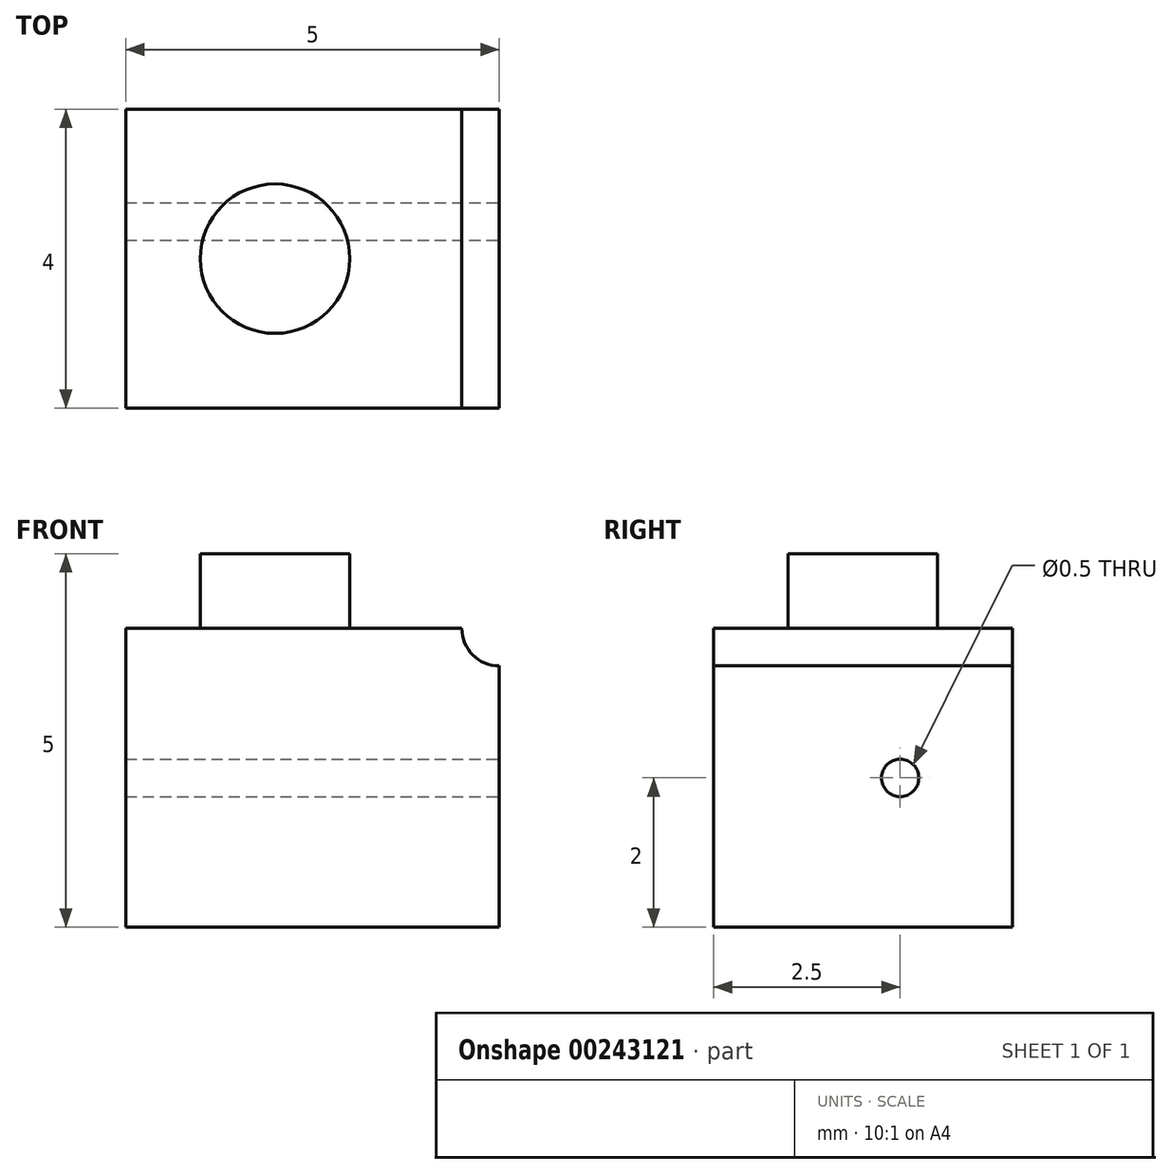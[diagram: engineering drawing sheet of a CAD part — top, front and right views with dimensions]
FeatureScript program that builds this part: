
annotation { "Feature Type Name" : "Feature", "Feature Type Description" : "" }
export const myFeature = defineFeature(function(context is Context, id is Id, definition is map)
    precondition{}
    {
        {
            var Q0;
            Q0=qCreatedBy(makeId("Top.planeOp"),FACE);
            var sketch = newSketch(context, id + "F0", { "sketchPlane" : qUnion([Q0])});
            skLineSegment(sketch, "E0", {"start": v(0, 0) * mm, "end": v(5, 0) * mm});
            skLineSegment(sketch, "E1", {"start": v(5, 0) * mm, "end": v(5, 4) * mm});
            skLineSegment(sketch, "E2", {"start": v(5, 4) * mm, "end": v(0, 4) * mm});
            skLineSegment(sketch, "E3", {"start": v(0, 4) * mm, "end": v(0, 0) * mm});
            skLineSegment(sketch, "E4", {"start": v(0, 4) * mm, "end": v(2, 4) * mm});
            skLineSegment(sketch, "E5", {"start": v(0, 4) * mm, "end": v(0, 2) * mm});
            skSolve(sketch);
        }
        {
            var Q0;
            Q0=makeQuery(id+"F0.imprint","IMPRINT",FACE,{"disambiguationData":[TD([[makeQuery(id+"F0.imprint","IMPRINT",EDGE,{"derivedFrom":sQuery(id+"F0.wireOp",EDGE,"E0")}),1.0]])]});
            extrude(context, id + "F1", {"entities" : qUnion([Q0]), "depth" : 4 * mm});
        }
        {
            var Q0;
            Q0=makeQuery(id+"F1.opExtrude","CAP_FACE",FACE,{"disambiguationData":[OSD([sQuery(id+"F0.wireOp",EDGE,"E0"),sQuery(id+"F0.wireOp",EDGE,"E1"),sQuery(id+"F0.wireOp",EDGE,"E2"),sQuery(id+"F0.wireOp",EDGE,"E3"),sQuery(id+"F0.wireOp",EDGE,"E4"),sQuery(id+"F0.wireOp",EDGE,"E5")])],"isStart":false});
            var sketch = newSketch(context, id + "F2", { "sketchPlane" : qUnion([Q0])});
            skLineSegment(sketch, "E6", {"start": v(0, 4) * mm, "end": v(2, 4) * mm});
            skLineSegment(sketch, "E7", {"start": v(0, 2) * mm, "end": v(2, 2) * mm});
            skCircle(sketch, "E8", {"center": v(2, 2) * mm, "radius": 1 * mm});
            skSolve(sketch);
        }
        {
            var Q0;
            Q0 = qSketchRegion(id + "F2", true);
            extrude(context, id + "F3", {"entities" : qUnion([Q0]), "operationType" : NewBodyOperationType.ADD, "depth" : 1 * mm});
        }
        {
            var Q0;
            Q0=makeQuery(id+"F1.opExtrude","SWEPT_FACE",FACE,{"disambiguationData":[OSD([sQuery(id+"F0.wireOp",EDGE,"E2"),sQuery(id+"F0.wireOp",EDGE,"E4")])]});
            var sketch = newSketch(context, id + "F4", { "sketchPlane" : qUnion([Q0])});
            skCircle(sketch, "E9", {"center": v(-5, 4) * mm, "radius": 0.5 * mm});
            skSolve(sketch);
        }
        {
            var Q0;
            Q0 = qSketchRegion(id + "F4", true);
            extrude(context, id + "F5", {"entities" : qUnion([Q0]), "operationType" : NewBodyOperationType.REMOVE, "oppositeDirection" : true, "depth" : 4 * mm});
        }
        {
            var Q0;
            Q0=makeQuery(id+"F1.opExtrude","SWEPT_FACE",FACE,{"disambiguationData":[OSD([sQuery(id+"F0.wireOp",EDGE,"E1")])]});
            var sketch = newSketch(context, id + "F6", { "sketchPlane" : qUnion([Q0])});
            skLineSegment(sketch, "E10", {"start": v(4, 3.5) * mm, "end": v(4, 2) * mm});
            skLineSegment(sketch, "E11", {"start": v(4, 2) * mm, "end": v(2.5, 2) * mm});
            skCircle(sketch, "E12", {"center": v(2.5, 2) * mm, "radius": 0.25 * mm});
            skSolve(sketch);
        }
        {
            var Q0;
            Q0 = qSketchRegion(id + "F6", true);
            extrude(context, id + "F7", {"entities" : qUnion([Q0]), "operationType" : NewBodyOperationType.REMOVE, "oppositeDirection" : true, "depth" : 25 * mm});
        }
    });
